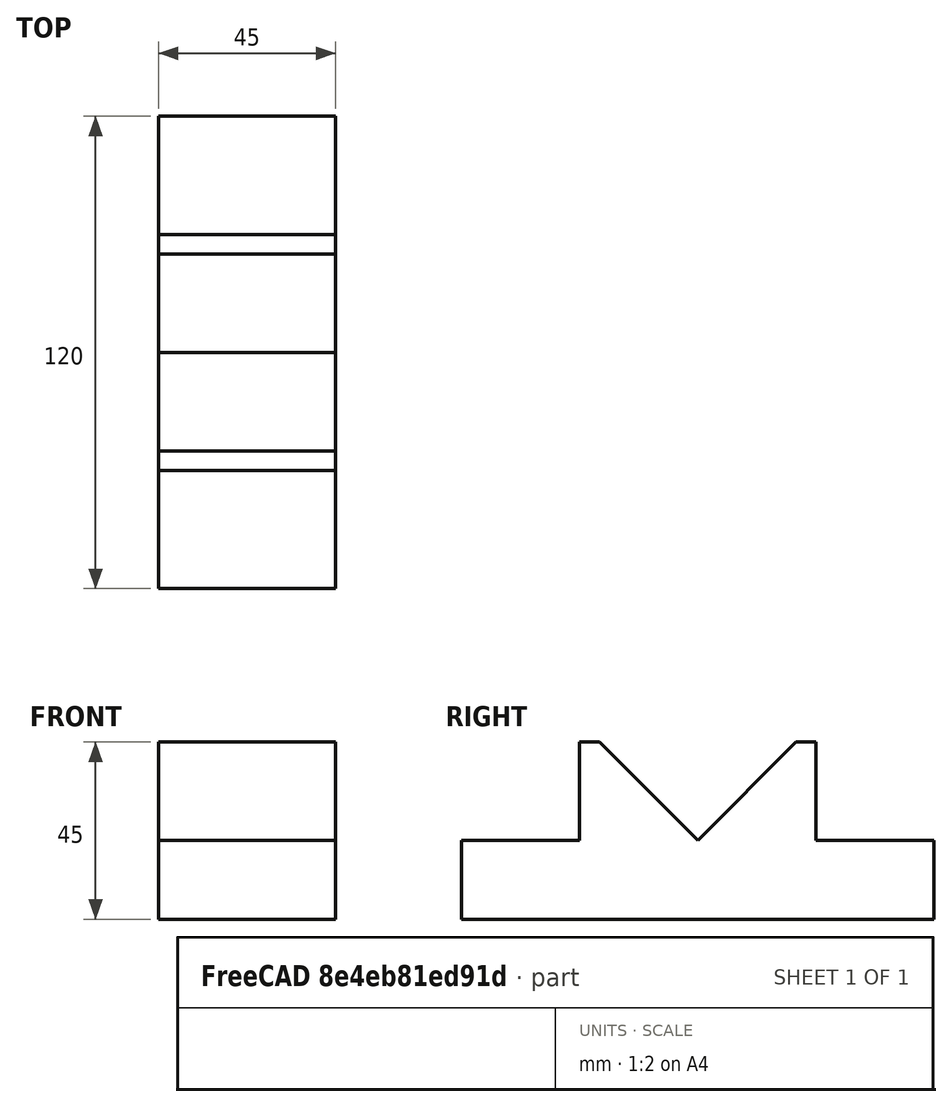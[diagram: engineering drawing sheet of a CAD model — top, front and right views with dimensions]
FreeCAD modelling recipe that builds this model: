
FCSTD DOCUMENT  (FreeCAD 0.18R4 (GitTag))
Label: BasicPart1
License: All rights reserved
LicenseURL: http://en.wikipedia.org/wiki/All_rights_reserved
objects: Sketcher::SketchObject×2, PartDesign::Pad×1, PartDesign::Body×1
note: 5 computed .brp shape members not serialized (recipe doc carries the construction recipe); baked Part::Feature solids carry a one-line shape summary decoded from their .brp

FEATURE [Sketcher::SketchObject] Sketch
  Placement = pos=(0,0,0) rot=(0.57735,0.57735,0.57735;2.0944rad)
  sketch-geometry (11):
    g0: LineSegment StartX=-60 StartY=0 StartZ=0 EndX=60 EndY=0 EndZ=0
    g1: LineSegment StartX=60 StartY=0 StartZ=0 EndX=60 EndY=20 EndZ=0
    g2: LineSegment StartX=60 StartY=20 StartZ=0 EndX=30 EndY=20 EndZ=0
    g3: LineSegment StartX=30 StartY=20 StartZ=0 EndX=30 EndY=45 EndZ=0
    g4: LineSegment StartX=30 StartY=45 StartZ=0 EndX=25 EndY=45 EndZ=0
    g5: LineSegment StartX=25 StartY=45 StartZ=0 EndX=0 EndY=20 EndZ=0
    g6: LineSegment StartX=0 StartY=20 StartZ=0 EndX=-25 EndY=45 EndZ=0
    g7: LineSegment StartX=-25 StartY=45 StartZ=0 EndX=-30 EndY=45 EndZ=0
    g8: LineSegment StartX=-30 StartY=45 StartZ=0 EndX=-30 EndY=20 EndZ=0
    g9: LineSegment StartX=-30 StartY=20 StartZ=0 EndX=-60 EndY=20 EndZ=0
    g10: LineSegment StartX=-60 StartY=20 StartZ=0 EndX=-60 EndY=0 EndZ=0
  constraints (30):
    c: Coincident(g0,g1)
    c: Coincident(g1,g2)
    c: Coincident(g2,g3)
    c: Coincident(g3,g4)
    c: Coincident(g4,g5)
    c: Coincident(g5,g6)
    c: Coincident(g6,g7)
    c: Coincident(g7,g8)
    c: Coincident(g8,g9)
    c: Coincident(g9,g10)
    c: Coincident(g10,g0)
    c: PointOnObject(g0,g-1)
    c: PointOnObject(g0,g-1)
    c: Vertical(g1)
    c: Vertical(g10)
    c: Horizontal(g2)
    c: Symmetric(g9,g1,g-2)
    c: Symmetric(g8,g2,g-2)
    c: Symmetric(g7,g3,g-2)
    c: Symmetric(g6,g4,g-2)
    c: PointOnObject(g5,g-2)
    c: Vertical(g8)
    c: Horizontal(g7)
    c: Angle(g5,g6) = 1.5708
    c: Distance(g9) = 30
    c: Distance(g1) = 20
    c: Equal(g8,g3)
    c: Distance(g3) = 25
    c: Distance(g7) = 5
    c: Distance(g0) = 120
FEATURE [Sketcher::SketchObject] CopySketch
  Placement = pos=(0,0,0) rot=(0.57735,0.57735,0.57735;2.0944rad)
  sketch-geometry (11):
    g0: LineSegment StartX=-60 StartY=0 StartZ=0 EndX=60 EndY=0 EndZ=0
    g1: LineSegment StartX=60 StartY=0 StartZ=0 EndX=60 EndY=20 EndZ=0
    g2: LineSegment StartX=60 StartY=20 StartZ=0 EndX=30 EndY=20 EndZ=0
    g3: LineSegment StartX=30 StartY=20 StartZ=0 EndX=30 EndY=45 EndZ=0
    g4: LineSegment StartX=30 StartY=45 StartZ=0 EndX=25 EndY=45 EndZ=0
    g5: LineSegment StartX=25 StartY=45 StartZ=0 EndX=0 EndY=20 EndZ=0
    g6: LineSegment StartX=0 StartY=20 StartZ=0 EndX=-25 EndY=45 EndZ=0
    g7: LineSegment StartX=-25 StartY=45 StartZ=0 EndX=-30 EndY=45 EndZ=0
    g8: LineSegment StartX=-30 StartY=45 StartZ=0 EndX=-30 EndY=20 EndZ=0
    g9: LineSegment StartX=-30 StartY=20 StartZ=0 EndX=-60 EndY=20 EndZ=0
    g10: LineSegment StartX=-60 StartY=20 StartZ=0 EndX=-60 EndY=0 EndZ=0
  constraints (30):
    c: Coincident(g0,g1)
    c: Coincident(g1,g2)
    c: Coincident(g2,g3)
    c: Coincident(g3,g4)
    c: Coincident(g4,g5)
    c: Coincident(g5,g6)
    c: Coincident(g6,g7)
    c: Coincident(g7,g8)
    c: Coincident(g8,g9)
    c: Coincident(g9,g10)
    c: Coincident(g10,g0)
    c: PointOnObject(g0,g-1)
    c: PointOnObject(g0,g-1)
    c: Vertical(g1)
    c: Vertical(g10)
    c: Horizontal(g2)
    c: Symmetric(g9,g1,g-2)
    c: Symmetric(g8,g2,g-2)
    c: Symmetric(g7,g3,g-2)
    c: Symmetric(g6,g4,g-2)
    c: PointOnObject(g5,g-2)
    c: Vertical(g8)
    c: Horizontal(g7)
    c: Angle(g5,g6) = 1.5708
    c: Distance(g9) = 30
    c: Distance(g1) = 20
    c: Equal(g8,g3)
    c: Distance(g3) = 25
    c: Distance(g7) = 5
    c: Distance(g0) = 120
FEATURE [PartDesign::Pad] Pad
  Length = 45
  Length2 = 100
  Midplane = true
  Placement = pos=(0,0,0) rot=(0.57735,0.57735,0.57735;2.0944rad)
  Profile = -> CopySketch
  Type = 0
FEATURE [PartDesign::Body] Body
  Group = -> [Pad]
  Origin = -> Origin
  Tip = -> Pad
